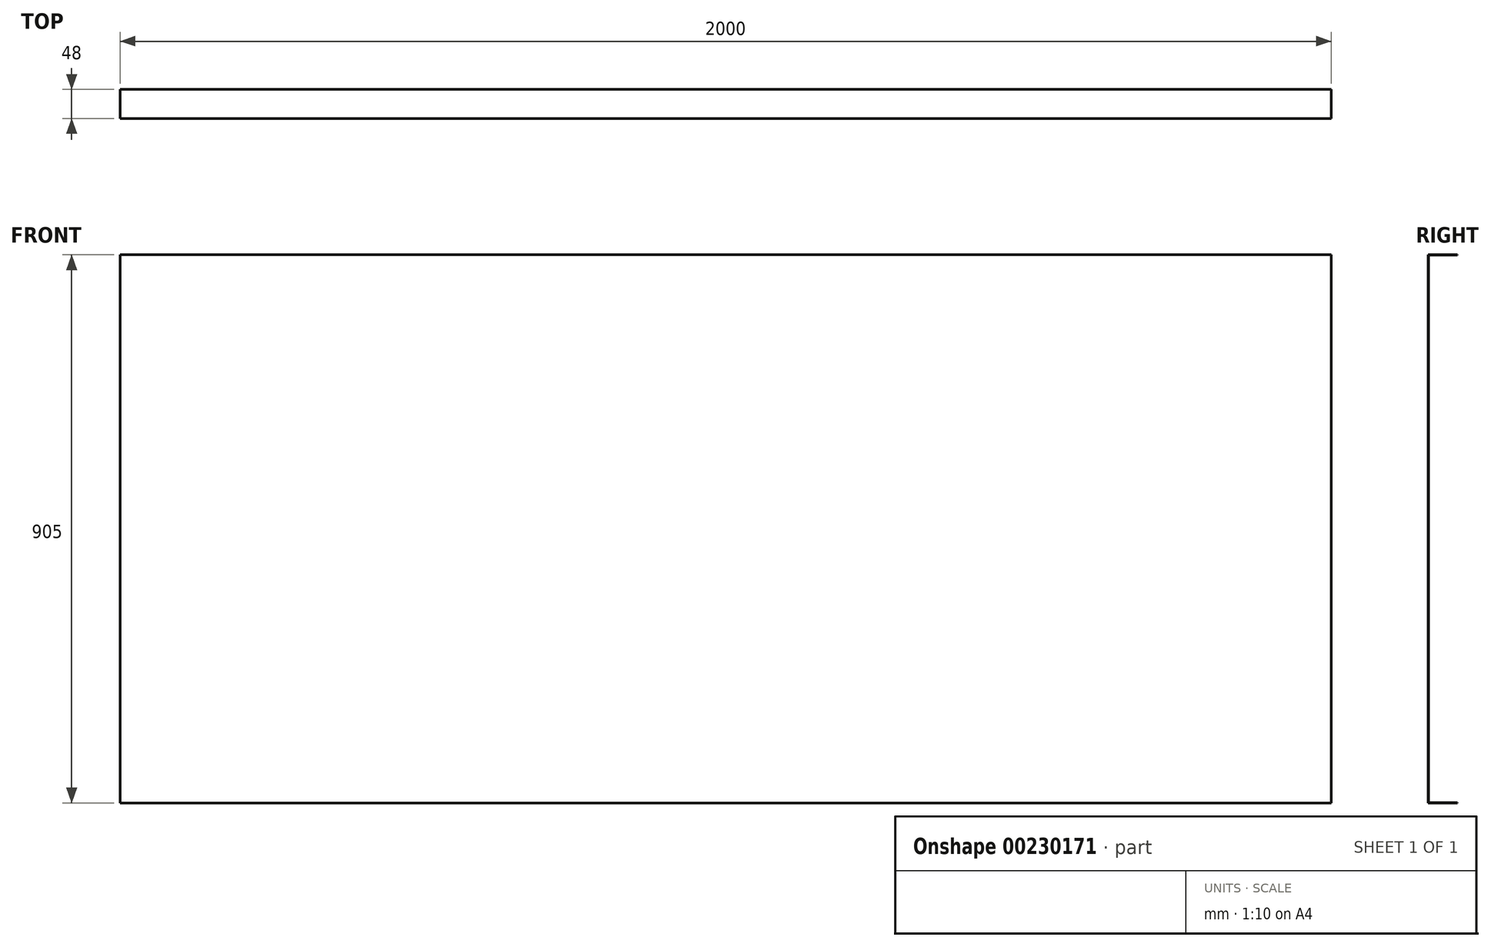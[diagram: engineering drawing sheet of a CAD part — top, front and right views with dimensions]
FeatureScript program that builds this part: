
annotation { "Feature Type Name" : "Feature", "Feature Type Description" : "" }
export const myFeature = defineFeature(function(context is Context, id is Id, definition is map)
    precondition{}
    {
        {
            var Q0;
            Q0=qCreatedBy(makeId("Front.planeOp"),FACE);
            var sketch = newSketch(context, id + "F0", { "sketchPlane" : qUnion([Q0])});
            skLineSegment(sketch, "E0.bottom", {"start": v(1941.38, 882.5) * mm, "end": v(-58.62, 882.5) * mm});
            skLineSegment(sketch, "E0.top", {"start": v(1941.38, -22.5) * mm, "end": v(-58.62, -22.5) * mm});
            skLineSegment(sketch, "E0.left", {"start": v(1941.38, 882.5) * mm, "end": v(1941.38, -22.5) * mm});
            skLineSegment(sketch, "E0.right", {"start": v(-58.62, 882.5) * mm, "end": v(-58.62, -22.5) * mm});
            skSolve(sketch);
        }
        {
            var Q0;
            Q0=makeQuery(id+"F0.imprint","IMPRINT",FACE,{"disambiguationData":[TD([[makeQuery(id+"F0.imprint","IMPRINT",EDGE,{"derivedFrom":sQuery(id+"F0.wireOp",EDGE,"E0.bottom")}),1.0]])]});
            extrude(context, id + "F1", {"entities" : qUnion([Q0]), "depth" : 0.5 * mm});
        }
        {
            var Q0;
            Q0=makeQuery(id+"F1.opExtrude","CAP_FACE",FACE,{"disambiguationData":[OSD([sQuery(id+"F0.wireOp",EDGE,"E0.bottom"),sQuery(id+"F0.wireOp",EDGE,"E0.top"),sQuery(id+"F0.wireOp",EDGE,"E0.left"),sQuery(id+"F0.wireOp",EDGE,"E0.right")])],"isStart":true});
            var sketch = newSketch(context, id + "F2", { "sketchPlane" : qUnion([Q0])});
            skLineSegment(sketch, "E1.bottom", {"start": v(58.62, 882.5) * mm, "end": v(-1941.38, 882.5) * mm});
            skLineSegment(sketch, "E1.top", {"start": v(58.62, 882.5) * mm, "end": v(-1941.38, 882.5) * mm});
            skLineSegment(sketch, "E1.left", {"start": v(58.62, 882.5) * mm, "end": v(58.62, 882.5) * mm});
            skLineSegment(sketch, "E1.right", {"start": v(-1941.38, 882.5) * mm, "end": v(-1941.38, 882.5) * mm});
            skLineSegment(sketch, "E2.bottom", {"start": v(-1941.38, 882.5) * mm, "end": v(58.62, 882.5) * mm});
            skLineSegment(sketch, "E2.top", {"start": v(-1941.38, 882.5) * mm, "end": v(58.62, 882.5) * mm});
            skLineSegment(sketch, "E3.top", {"start": v(-1941.38, 882) * mm, "end": v(58.62, 882) * mm});
            skLineSegment(sketch, "E3.left", {"start": v(-1941.38, 882.5) * mm, "end": v(-1941.38, 882) * mm});
            skLineSegment(sketch, "E3.right", {"start": v(58.62, 882.5) * mm, "end": v(58.62, 882) * mm});
            skLineSegment(sketch, "E4.bottom", {"start": v(-1941.38, -22.5) * mm, "end": v(58.62, -22.5) * mm});
            skLineSegment(sketch, "E4.top", {"start": v(-1941.38, -22) * mm, "end": v(58.62, -22) * mm});
            skLineSegment(sketch, "E4.left", {"start": v(-1941.38, -22.5) * mm, "end": v(-1941.38, -22) * mm});
            skLineSegment(sketch, "E4.right", {"start": v(58.62, -22.5) * mm, "end": v(58.62, -22) * mm});
            skSolve(sketch);
        }
        {
            var Q0;
            Q0 = qSketchRegion(id + "F2", true);
            extrude(context, id + "F3", {"entities" : qUnion([Q0]), "operationType" : NewBodyOperationType.ADD, "depth" : 47.5 * mm});
        }
    });
